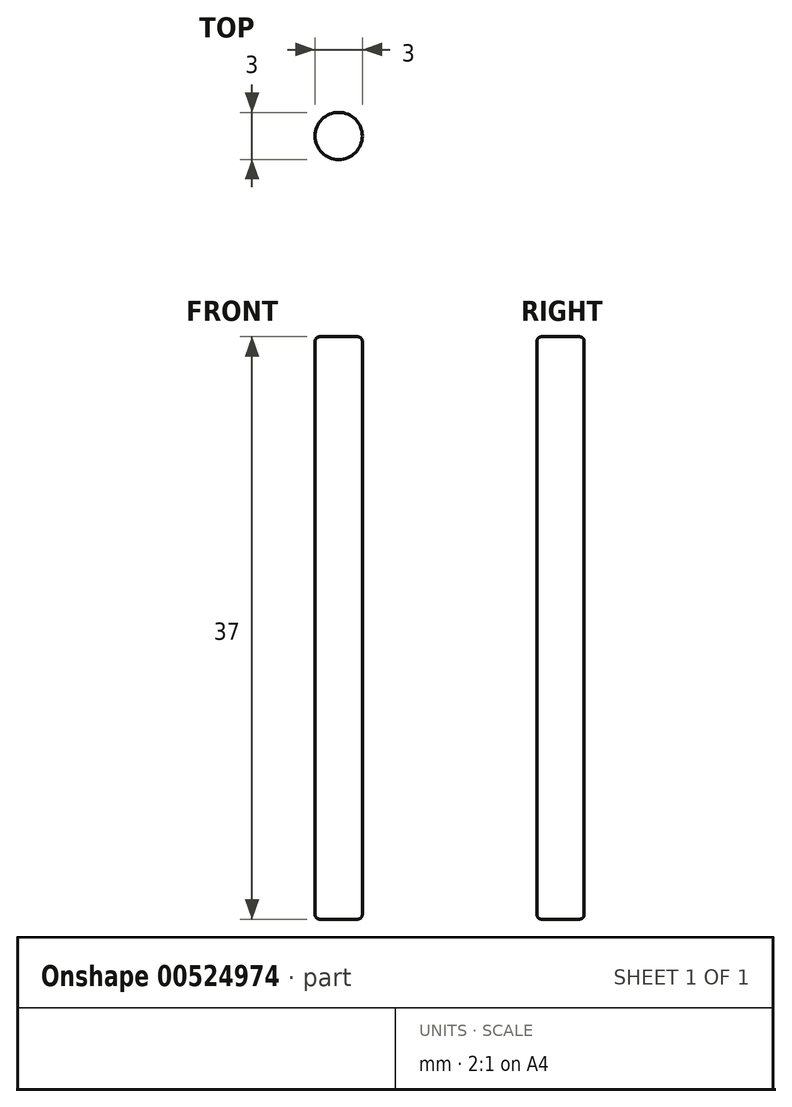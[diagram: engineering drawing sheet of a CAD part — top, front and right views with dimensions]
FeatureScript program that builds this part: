
annotation { "Feature Type Name" : "Feature", "Feature Type Description" : "" }
export const myFeature = defineFeature(function(context is Context, id is Id, definition is map)
    precondition{}
    {
        {
            var Q0;
            Q0=qCreatedBy(makeId("Top.planeOp"),FACE);
            var sketch = newSketch(context, id + "F0", { "sketchPlane" : qUnion([Q0])});
            skCircle(sketch, "E0", {"center": v(0, 0) * mm, "radius": 1.5 * mm});
            skSolve(sketch);
        }
        {
            var Q0;
            Q0=makeQuery(id+"F0.imprint","IMPRINT",FACE,{"disambiguationData":[TD([[makeQuery(id+"F0.imprint","IMPRINT",EDGE,{"derivedFrom":sQuery(id+"F0.wireOp",EDGE,"E0")}),1.0]])]});
            extrude(context, id + "F1", {"entities" : qUnion([Q0]), "depth" : 37 * mm, "offsetDistance" : 25 * mm});
        }
        {
            var Q0;
            Q0=makeQuery(id+"F1.opExtrude","CAP_EDGE",EDGE,{"disambiguationData":[OSD([sQuery(id+"F0.wireOp",EDGE,"E0")])],"isStart":false});
            var Q1;
            Q1=makeQuery(id+"F1.opExtrude","CAP_EDGE",EDGE,{"disambiguationData":[OSD([sQuery(id+"F0.wireOp",EDGE,"E0")])],"isStart":true});
            fillet(context, id + "F2", {"entities" : qUnion([Q0, Q1]), "radius" : 0.3 * mm, "tangentPropagation" : true, "allowEdgeOverflow" : false});
        }
    });
